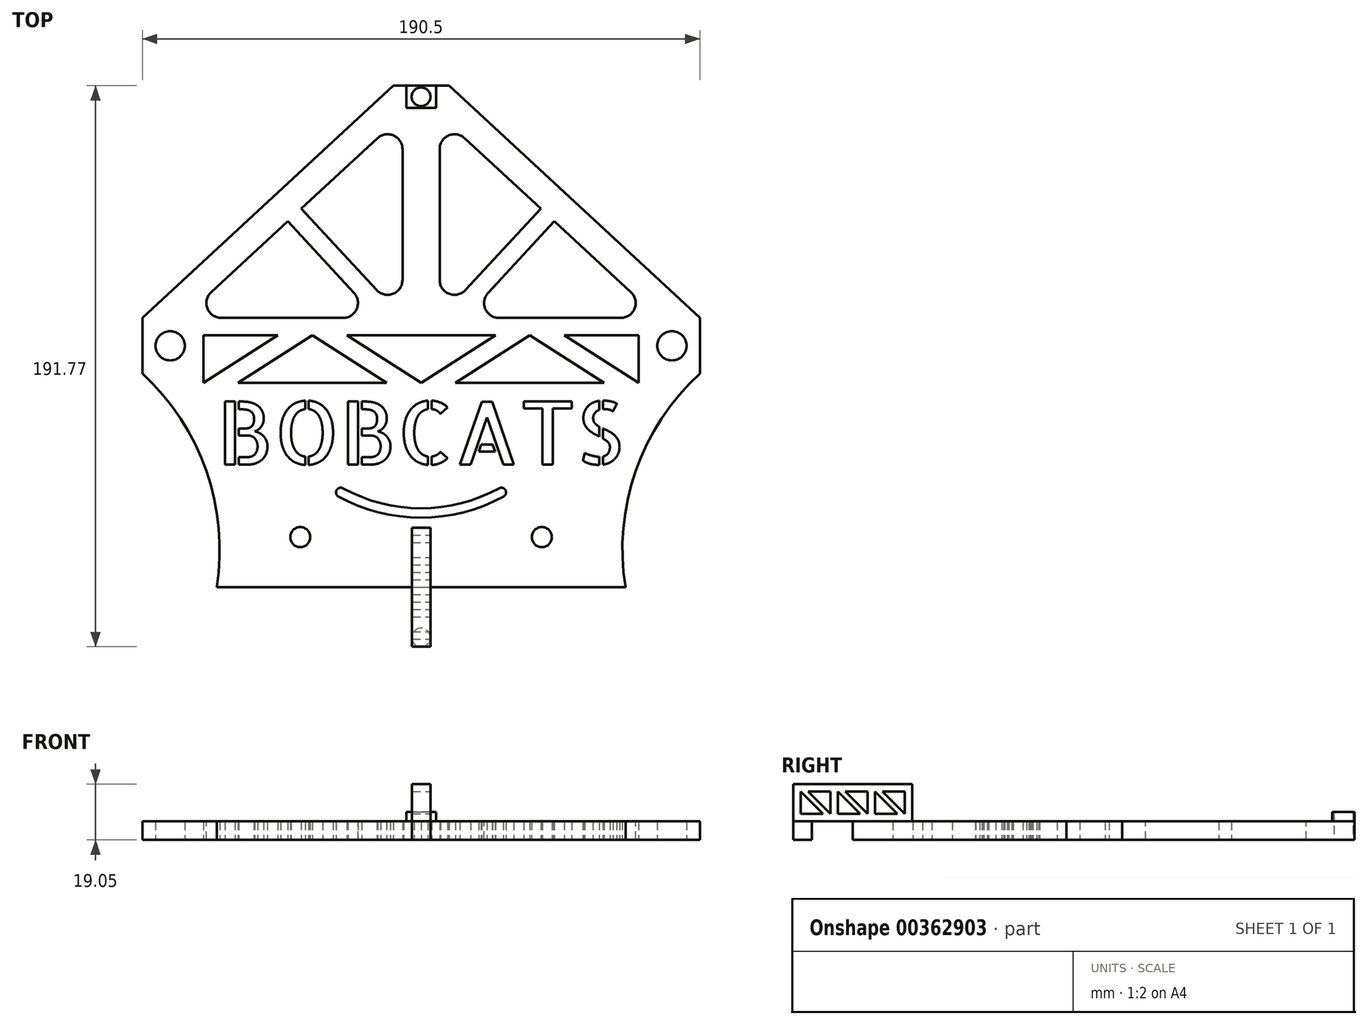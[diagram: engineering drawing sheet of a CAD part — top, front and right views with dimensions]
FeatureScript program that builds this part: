
annotation { "Feature Type Name" : "Feature", "Feature Type Description" : "" }
export const myFeature = defineFeature(function(context is Context, id is Id, definition is map)
    precondition{}
    {
        {
            var Q0;
            Q0=qCreatedBy(makeId("Top.planeOp"),FACE);
            var sketch = newSketch(context, id + "F0", { "sketchPlane" : qUnion([Q0])});
            skLineSegment(sketch, "E0.bottom", {"start": v(-9.53, 88.9) * mm, "end": v(9.53, 88.9) * mm});
            skLineSegment(sketch, "E0.top", {"start": v(-69.85, -82.55) * mm, "end": v(69.85, -82.55) * mm});
            skLineSegment(sketch, "E0.left", {"start": v(-95.25, 9.53) * mm, "end": v(-95.25, -9.52) * mm});
            skLineSegment(sketch, "E0.right", {"start": v(95.25, 9.53) * mm, "end": v(95.25, -9.52) * mm});
            skPoint(sketch, "E0.middle", {"position": v(0, 0) * mm});
            skLineSegment(sketch, "E1", {"start": v(-9.53, 88.9) * mm, "end": v(-95.25, 9.53) * mm});
            skLineSegment(sketch, "E2", {"start": v(9.53, 88.9) * mm, "end": v(95.25, 9.53) * mm});
            skCircle(sketch, "E3", {"center": v(-85.73, 0) * mm, "radius": 5 * mm});
            skCircle(sketch, "E4", {"center": v(85.73, 0) * mm, "radius": 5 * mm});
            skLineSegment(sketch, "E5", {"start": v(-95.25, -9.52) * mm, "end": v(-69.85, -82.55) * mm});
            skLineSegment(sketch, "E6", {"start": v(95.25, -9.52) * mm, "end": v(69.85, -82.55) * mm});
            skPoint(sketch, "E7", {"position": v(0, 85.1) * mm});
            skPoint(sketch, "E7.positionSnap0", {"position": v(0, 88.9) * mm});
            skCircle(sketch, "E8", {"center": v(0, 85.1) * mm, "radius": 3.2 * mm});
            skLineSegment(sketch, "E9.bottom", {"start": v(-5.08, 88.9) * mm, "end": v(5.08, 88.9) * mm});
            skLineSegment(sketch, "E9.top", {"start": v(-5.08, 81.28) * mm, "end": v(5.08, 81.28) * mm});
            skLineSegment(sketch, "E9.left", {"start": v(-5.08, 88.9) * mm, "end": v(-5.08, 81.28) * mm});
            skLineSegment(sketch, "E9.right", {"start": v(5.08, 88.9) * mm, "end": v(5.08, 81.28) * mm});
            skPoint(sketch, "E10", {"position": v(0, -82.55) * mm});
            skPoint(sketch, "E11", {"position": v(-95.25, 0) * mm});
            skPoint(sketch, "E12", {"position": v(95.25, 0) * mm});
            skLineSegment(sketch, "E13", {"start": v(0, 6.08) * mm, "end": v(0, -88.82) * mm, "construction": true});
            skCircle(sketch, "E14", {"center": v(41.28, -65.4) * mm, "radius": 3.43 * mm});
            skCircle(sketch, "E15.MirrorC", {"center": v(-41.27, -65.4) * mm, "radius": 3.43 * mm});
            skText(sketch, "E16", { "text": "BOBCATS", "fontName": "AllertaStencil-Regular.ttf"});
            skLineSegment(sketch, "E17", {"start": v(6.35, 78.86) * mm, "end": v(40.91, 46.85) * mm});
            skLineSegment(sketch, "E18", {"start": v(40.91, 46.85) * mm, "end": v(6.35, 9.52) * mm});
            skLineSegment(sketch, "E19", {"start": v(6.35, 9.52) * mm, "end": v(6.35, 78.86) * mm});
            skLineSegment(sketch, "E20", {"start": v(45.57, 42.54) * mm, "end": v(15, 9.52) * mm});
            skLineSegment(sketch, "E21", {"start": v(15, 9.52) * mm, "end": v(81.23, 9.53) * mm});
            skLineSegment(sketch, "E22", {"start": v(81.23, 9.52) * mm, "end": v(45.57, 42.54) * mm});
            skLineSegment(sketch, "E23.MirrorCS", {"start": v(-15, 9.52) * mm, "end": v(-81.23, 9.53) * mm});
            skLineSegment(sketch, "E24.MirrorCS", {"start": v(-81.23, 9.52) * mm, "end": v(-45.57, 42.54) * mm});
            skLineSegment(sketch, "E25.MirrorCS", {"start": v(-45.57, 42.54) * mm, "end": v(-15, 9.52) * mm});
            skLineSegment(sketch, "E26.MirrorCS", {"start": v(-6.35, 9.52) * mm, "end": v(-6.35, 78.86) * mm});
            skLineSegment(sketch, "E27.MirrorCS", {"start": v(-40.91, 46.85) * mm, "end": v(-6.35, 9.52) * mm});
            skLineSegment(sketch, "E28.MirrorCS", {"start": v(-6.35, 78.86) * mm, "end": v(-40.91, 46.85) * mm});
            skLineSegment(sketch, "E29", {"start": v(-25.4, 3.6) * mm, "end": v(25.4, 3.6) * mm});
            skLineSegment(sketch, "E30", {"start": v(25.4, 3.6) * mm, "end": v(0, -12.7) * mm});
            skLineSegment(sketch, "E31", {"start": v(0, -12.7) * mm, "end": v(-25.4, 3.6) * mm});
            skLineSegment(sketch, "E32", {"start": v(-37.16, 3.6) * mm, "end": v(-11.76, -12.7) * mm});
            skLineSegment(sketch, "E33", {"start": v(-11.76, -12.7) * mm, "end": v(-62.56, -12.7) * mm});
            skLineSegment(sketch, "E34", {"start": v(-62.56, -12.7) * mm, "end": v(-37.16, 3.6) * mm});
            skLineSegment(sketch, "E35", {"start": v(-48.91, 3.6) * mm, "end": v(-74.31, -12.7) * mm});
            skLineSegment(sketch, "E36", {"start": v(-74.31, -12.7) * mm, "end": v(-74.31, 3.6) * mm});
            skLineSegment(sketch, "E37", {"start": v(-74.31, 3.6) * mm, "end": v(-48.91, 3.6) * mm});
            skLineSegment(sketch, "E38.MirrorCS", {"start": v(37.16, 3.6) * mm, "end": v(11.76, -12.7) * mm});
            skLineSegment(sketch, "E39.MirrorCS", {"start": v(11.76, -12.7) * mm, "end": v(62.56, -12.7) * mm});
            skLineSegment(sketch, "E40.MirrorCS", {"start": v(62.56, -12.7) * mm, "end": v(37.16, 3.6) * mm});
            skLineSegment(sketch, "E41.MirrorCS", {"start": v(74.31, 3.6) * mm, "end": v(48.91, 3.6) * mm});
            skLineSegment(sketch, "E42.MirrorCS", {"start": v(48.91, 3.6) * mm, "end": v(74.31, -12.7) * mm});
            skLineSegment(sketch, "E43.MirrorCS", {"start": v(74.31, -12.7) * mm, "end": v(74.31, 3.6) * mm});
            skArc(sketch, "E44", {"start": v(-69.85, -82.55) * mm, "mid": v(-73.32, -42.83) * mm, "end": v(-95.25, -9.52) * mm});
            skArc(sketch, "E45.MirrorCS", {"start": v(69.85, -82.55) * mm, "mid": v(73.32, -42.83) * mm, "end": v(95.25, -9.52) * mm});
            skLineSegment(sketch, "E46", {"start": v(-27.46, -50.12) * mm, "end": v(30.48, -50.12) * mm, "construction": true});
            skArc(sketch, "E47", {"start": v(-27.46, -50.12) * mm, "mid": v(0, -57.15) * mm, "end": v(27.46, -50.12) * mm, "construction": true});
            skArc(sketch, "E48.0", {"start": v(-26.7, -48.72) * mm, "mid": v(0, -55.55) * mm, "end": v(26.7, -48.72) * mm});
            skArc(sketch, "E49.0", {"start": v(-28.23, -51.52) * mm, "mid": v(0, -58.75) * mm, "end": v(28.23, -51.52) * mm});
            skCircle(sketch, "E50", {"center": v(-27.46, -50.12) * mm, "radius": 1.6 * mm});
            skCircle(sketch, "E51", {"center": v(27.46, -50.12) * mm, "radius": 1.6 * mm});
            const initialGuessF0  = {"E16": [-0.06985, -0.0406, 1, 0, 0.02154]};
            skSetInitialGuess(sketch, initialGuessF0);
            skSolve(sketch);
        }
        {
            var Q0;
            {var subQ1=sQuery(id+"F0.wireOp",EDGE,"E0.top");Q0=makeQuery(id+"F0.imprint","IMPRINT",FACE,{"disambiguationData":[TD([[makeQuery(id+"F0.imprint","IMPRINT",EDGE,{"derivedFrom":subQ1}),1.0]])]});}
            extrude(context, id + "F1", {"entities" : qUnion([Q0]), "depth" : 6.35 * mm});
        }
        {
            var Q0;
            Q0=makeQuery(id+"F1.opExtrude","CAP_FACE",FACE,{"disambiguationData":[OSD([sQuery(id+"F0.wireOp",EDGE,"E0.bottom"),sQuery(id+"F0.wireOp",EDGE,"E0.top"),sQuery(id+"F0.wireOp",EDGE,"E0.left"),sQuery(id+"F0.wireOp",EDGE,"E0.right"),sQuery(id+"F0.wireOp",EDGE,"E1"),sQuery(id+"F0.wireOp",EDGE,"E2"),sQuery(id+"F0.wireOp",EDGE,"E3"),sQuery(id+"F0.wireOp",EDGE,"E4"),sQuery(id+"F0.wireOp",EDGE,"E5"),sQuery(id+"F0.wireOp",EDGE,"E6"),sQuery(id+"F0.wireOp",EDGE,"E9.top"),sQuery(id+"F0.wireOp",EDGE,"E9.left"),sQuery(id+"F0.wireOp",EDGE,"E9.right"),sQuery(id+"F0.wireOp",EDGE,"WK9Ge9eX-SFjL-Fqqy-Bi8B-BWZohPfzdW64"),sQuery(id+"F0.wireOp",EDGE,"cjfLoNjD-HGCj-0mg2-fxAi-RncJ5tnOWQYy"),sQuery(id+"F0.wireOp",EDGE,"hTjJeYC6-jtfH-sRj1-Ofla-BOZ5YTjWMUSR"),sQuery(id+"F0.wireOp",EDGE,"F0UQwizI-j6N1-x3rF-HeOX-vzJCNuBWRCFr"),sQuery(id+"F0.wireOp",EDGE,"b4IquGWf-orqd-uga3-UJKT-QLBsU3ZspvGq"),sQuery(id+"F0.wireOp",EDGE,"wIZt3HxT-JghX-iFXP-RwIO-mji1NXU4TtsK"),sQuery(id+"F0.wireOp",EDGE,"3jfMUB13-TVLv-CSPL-KZ5n-4lXZqUwgOWmo"),sQuery(id+"F0.wireOp",EDGE,"pVTuvMID-cSwe-xcCd-8Qpg-RxuYvy9kya1v"),sQuery(id+"F0.wireOp",EDGE,"EFtgUnEl-t4Mr-Whu5-3tls-J0aPLypJ9zu3"),sQuery(id+"F0.wireOp",EDGE,"1cZBuPLp-VnRa-zOLz-okvN-oppCfpEN7lrB"),sQuery(id+"F0.wireOp",EDGE,"TxowZLdJ-HzB3-KTwi-xOqH-K86OHwTXBLWI"),sQuery(id+"F0.wireOp",EDGE,"LFEPvA81-wZiz-RjWD-FMGw-ZHGAvMGq3D5c"),sQuery(id+"F0.wireOp",EDGE,"Dv0HlwtA-8wQH-enx5-O6s7-vBL2QpsMf9wj")])],"isStart":false});
            var sketch = newSketch(context, id + "F2", { "sketchPlane" : qUnion([Q0])});
            skLineSegment(sketch, "E52.bottom", {"start": v(-3.17, -62.23) * mm, "end": v(3.18, -62.23) * mm});
            skLineSegment(sketch, "E52.top", {"start": v(-3.17, -102.87) * mm, "end": v(3.18, -102.87) * mm});
            skLineSegment(sketch, "E52.left", {"start": v(-3.17, -62.23) * mm, "end": v(-3.17, -102.87) * mm});
            skLineSegment(sketch, "E52.right", {"start": v(3.18, -62.23) * mm, "end": v(3.18, -102.87) * mm});
            skPoint(sketch, "E52.middle", {"position": v(0, -82.55) * mm});
            skSolve(sketch);
        }
        {
            var Q0;
            Q0=makeQuery(id+"F0.imprint","IMPRINT",FACE,{"disambiguationData":[TD([[makeQuery(id+"F0.imprint","IMPRINT",EDGE,{"derivedFrom":sQuery(id+"F0.wireOp",EDGE,"E8")}),-1.0]])]});
            extrude(context, id + "F3", {"entities" : qUnion([Q0]), "operationType" : NewBodyOperationType.ADD, "depth" : 9.52 * mm});
        }
        {
            var Q0;
            {var subQ0=sQuery(id+"F2.wireOp",EDGE,"E52.bottom");Q0=makeQuery(id+"F2.imprint","IMPRINT",FACE,{"disambiguationData":[TD([[makeQuery(id+"F2.imprint","IMPRINT",EDGE,{"derivedFrom":subQ0}),-1.0]])]});}
            var Q1;
            {var subQ0=sQuery(id+"F2.wireOp",EDGE,"E52.top");Q1=makeQuery(id+"F2.imprint","IMPRINT",FACE,{"disambiguationData":[TD([[makeQuery(id+"F2.imprint","IMPRINT",EDGE,{"derivedFrom":subQ0}),1.0]])]});}
            extrude(context, id + "F4", {"entities" : qUnion([Q0, Q1]), "operationType" : NewBodyOperationType.ADD, "depth" : 12.7 * mm});
        }
        {
            var Q0;
            Q0=makeQuery(id+"F4.opExtrude","CAP_FACE",FACE,{"disambiguationData":[OSD([sQuery(id+"F2.wireOp",EDGE,"E52.bottom"),sQuery(id+"F2.wireOp",EDGE,"E52.top"),sQuery(id+"F2.wireOp",EDGE,"E52.left"),sQuery(id+"F2.wireOp",EDGE,"E52.right")])],"isStart":true});
            var sketch = newSketch(context, id + "F5", { "sketchPlane" : qUnion([Q0])});
            skCircle(sketch, "E53", {"center": v(0, 99.7) * mm, "radius": 3.18 * mm});
            skSolve(sketch);
        }
        {
            var Q0;
            {var subQ0=sQuery(id+"F5.wireOp",EDGE,"E53");var subQ1=sQuery(id+"F2.wireOp",EDGE,"E52.top");var subQ2=makeQuery(id+"F5.imprint","INTERSECT",VERTEX,{"derivedFrom":[makeQuery(id+"F4.opExtrude","CAP_EDGE",EDGE,{"disambiguationData":[OSD([subQ1])],"isStart":true}),subQ0]});Q0=makeQuery(id+"F5.imprint","IMPRINT",FACE,{"disambiguationData":[TD([[makeQuery(id+"F5.imprint","IMPRINT",EDGE,{"disambiguationData":[TD([[subQ2,1.0]])],"derivedFrom":subQ0}),1.0]])]});}
            extrude(context, id + "F6", {"entities" : qUnion([Q0]), "operationType" : NewBodyOperationType.ADD, "depth" : 6.35 * mm});
        }
        {
            var Q0;
            Q0=makeQuery(id+"F4.opExtrude","SWEPT_FACE",FACE,{"disambiguationData":[OSD([sQuery(id+"F2.wireOp",EDGE,"E52.right")])]});
            var sketch = newSketch(context, id + "F7", { "sketchPlane" : qUnion([Q0])});
            skLineSegment(sketch, "E54", {"start": v(-100.33, 16.51) * mm, "end": v(-100.33, 8.9) * mm});
            skLineSegment(sketch, "E55", {"start": v(-100.33, 8.89) * mm, "end": v(-92.71, 8.89) * mm});
            skLineSegment(sketch, "E56", {"start": v(-92.71, 8.89) * mm, "end": v(-100.33, 16.51) * mm});
            skLineSegment(sketch, "E57", {"start": v(-97.8, 16.51) * mm, "end": v(-90.17, 8.9) * mm});
            skLineSegment(sketch, "E58", {"start": v(-90.17, 8.9) * mm, "end": v(-90.17, 16.51) * mm});
            skLineSegment(sketch, "E59", {"start": v(-90.17, 16.51) * mm, "end": v(-97.8, 16.51) * mm});
            skLineSegment(sketch, "E60.1.0.0", {"start": v(-77.47, 8.9) * mm, "end": v(-77.47, 16.51) * mm});
            skLineSegment(sketch, "E60.1.0.1", {"start": v(-85.1, 16.51) * mm, "end": v(-77.47, 8.9) * mm});
            skLineSegment(sketch, "E60.1.0.2", {"start": v(-77.47, 16.51) * mm, "end": v(-85.1, 16.51) * mm});
            skLineSegment(sketch, "E60.1.0.3", {"start": v(-80.01, 8.89) * mm, "end": v(-87.63, 16.51) * mm});
            skLineSegment(sketch, "E60.1.0.4", {"start": v(-87.63, 16.51) * mm, "end": v(-87.63, 8.9) * mm});
            skLineSegment(sketch, "E60.1.0.5", {"start": v(-87.63, 8.89) * mm, "end": v(-80.01, 8.89) * mm});
            skLineSegment(sketch, "E60.2.0.0", {"start": v(-64.77, 8.9) * mm, "end": v(-64.77, 16.51) * mm});
            skLineSegment(sketch, "E60.2.0.1", {"start": v(-72.4, 16.51) * mm, "end": v(-64.77, 8.9) * mm});
            skLineSegment(sketch, "E60.2.0.2", {"start": v(-64.77, 16.51) * mm, "end": v(-72.4, 16.51) * mm});
            skLineSegment(sketch, "E60.2.0.3", {"start": v(-67.31, 8.89) * mm, "end": v(-74.93, 16.51) * mm});
            skLineSegment(sketch, "E60.2.0.4", {"start": v(-74.93, 16.51) * mm, "end": v(-74.93, 8.9) * mm});
            skLineSegment(sketch, "E60.2.0.5", {"start": v(-74.93, 8.89) * mm, "end": v(-67.31, 8.89) * mm});
            skLineSegment(sketch, "E60.direction1", {"start": v(-90.17, 8.9) * mm, "end": v(-77.47, 8.9) * mm, "construction": true});
            skSolve(sketch);
        }
        {
            var Q0;
            Q0=makeQuery(id+"F7.imprint","IMPRINT",FACE,{"disambiguationData":[TD([[makeQuery(id+"F7.imprint","IMPRINT",EDGE,{"derivedFrom":sQuery(id+"F7.wireOp",EDGE,"E54")}),1.0]])]});
            var Q1;
            Q1=makeQuery(id+"F7.imprint","IMPRINT",FACE,{"disambiguationData":[TD([[makeQuery(id+"F7.imprint","IMPRINT",EDGE,{"derivedFrom":sQuery(id+"F7.wireOp",EDGE,"E57")}),1.0]])]});
            var Q2;
            Q2=makeQuery(id+"F7.imprint","IMPRINT",FACE,{"disambiguationData":[TD([[makeQuery(id+"F7.imprint","IMPRINT",EDGE,{"derivedFrom":sQuery(id+"F7.wireOp",EDGE,"E60.1.0.3")}),1.0]])]});
            var Q3;
            Q3=makeQuery(id+"F7.imprint","IMPRINT",FACE,{"disambiguationData":[TD([[makeQuery(id+"F7.imprint","IMPRINT",EDGE,{"derivedFrom":sQuery(id+"F7.wireOp",EDGE,"E60.1.0.0")}),1.0]])]});
            var Q4;
            Q4=makeQuery(id+"F7.imprint","IMPRINT",FACE,{"disambiguationData":[TD([[makeQuery(id+"F7.imprint","IMPRINT",EDGE,{"derivedFrom":sQuery(id+"F7.wireOp",EDGE,"E60.2.0.3")}),1.0]])]});
            var Q5;
            Q5=makeQuery(id+"F7.imprint","IMPRINT",FACE,{"disambiguationData":[TD([[makeQuery(id+"F7.imprint","IMPRINT",EDGE,{"derivedFrom":sQuery(id+"F7.wireOp",EDGE,"E60.2.0.0")}),1.0]])]});
            extrude(context, id + "F8", {"entities" : qUnion([Q0, Q1, Q2, Q3, Q4, Q5]), "operationType" : NewBodyOperationType.REMOVE, "endBound" : BoundingType.THROUGH_ALL, "oppositeDirection" : true, "depth" : 25.4 * mm});
        }
        {
            var Q0;
            Q0=makeQuery(id+"F1.opExtrude","SWEPT_EDGE",EDGE,{"disambiguationData":[OSD([sQuery(id+"F0.wireOp",EDGE,"E18"),sQuery(id+"F0.wireOp",EDGE,"E19")])]});
            var Q1;
            Q1=makeQuery(id+"F1.opExtrude","SWEPT_EDGE",EDGE,{"disambiguationData":[OSD([sQuery(id+"F0.wireOp",EDGE,"E26.MirrorCS"),sQuery(id+"F0.wireOp",EDGE,"E27.MirrorCS")])]});
            var Q2;
            Q2=makeQuery(id+"F1.opExtrude","SWEPT_EDGE",EDGE,{"disambiguationData":[OSD([sQuery(id+"F0.wireOp",EDGE,"E26.MirrorCS"),sQuery(id+"F0.wireOp",EDGE,"E28.MirrorCS")])]});
            var Q3;
            Q3=makeQuery(id+"F1.opExtrude","SWEPT_EDGE",EDGE,{"disambiguationData":[OSD([sQuery(id+"F0.wireOp",EDGE,"E17"),sQuery(id+"F0.wireOp",EDGE,"E19")])]});
            var Q4;
            Q4=makeQuery(id+"F1.opExtrude","SWEPT_EDGE",EDGE,{"disambiguationData":[OSD([sQuery(id+"F0.wireOp",EDGE,"E20"),sQuery(id+"F0.wireOp",EDGE,"E21")])]});
            var Q5;
            Q5=makeQuery(id+"F1.opExtrude","SWEPT_EDGE",EDGE,{"disambiguationData":[OSD([sQuery(id+"F0.wireOp",EDGE,"E23.MirrorCS"),sQuery(id+"F0.wireOp",EDGE,"E25.MirrorCS")])]});
            var Q6;
            Q6=makeQuery(id+"F1.opExtrude","SWEPT_EDGE",EDGE,{"disambiguationData":[OSD([sQuery(id+"F0.wireOp",EDGE,"E23.MirrorCS"),sQuery(id+"F0.wireOp",EDGE,"E24.MirrorCS")])]});
            var Q7;
            Q7=makeQuery(id+"F1.opExtrude","SWEPT_EDGE",EDGE,{"disambiguationData":[OSD([sQuery(id+"F0.wireOp",EDGE,"E21"),sQuery(id+"F0.wireOp",EDGE,"E22")])]});
            fillet(context, id + "F9", {"entities" : qUnion([Q0, Q1, Q2, Q3, Q4, Q5, Q6, Q7]), "radius" : 5.08 * mm, "tangentPropagation" : true, "allowEdgeOverflow" : false});
        }
    });
